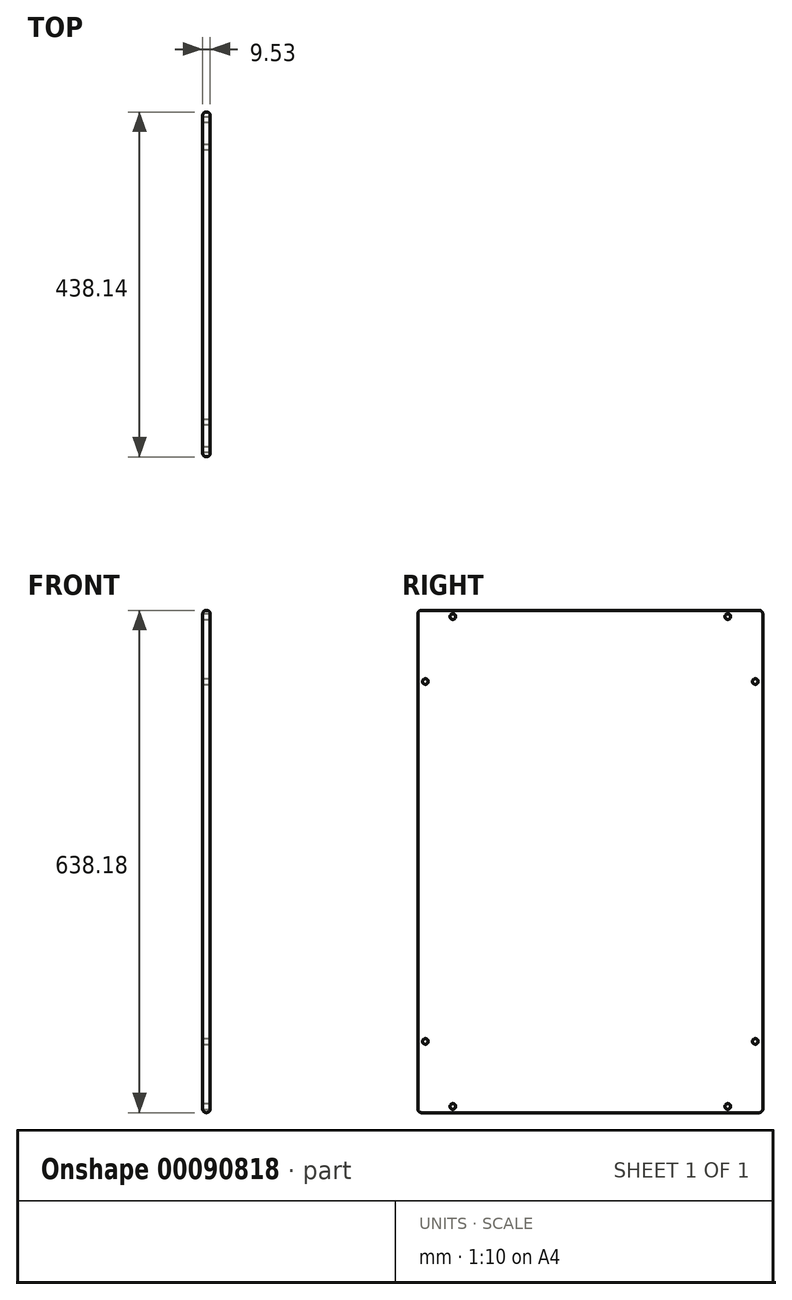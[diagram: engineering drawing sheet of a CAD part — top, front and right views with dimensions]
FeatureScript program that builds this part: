
annotation { "Feature Type Name" : "Feature", "Feature Type Description" : "" }
export const myFeature = defineFeature(function(context is Context, id is Id, definition is map)
    precondition{}
    {
        {
            var Q0;
            Q0=qCreatedBy(makeId("Right.planeOp"),FACE);
            var sketch = newSketch(context, id + "F0", { "sketchPlane" : qUnion([Q0])});
            skLineSegment(sketch, "E0.bottom", {"start": v(219.08, -319.09) * mm, "end": v(-219.07, -319.09) * mm});
            skLineSegment(sketch, "E0.top", {"start": v(219.07, 319.09) * mm, "end": v(-219.08, 319.09) * mm});
            skLineSegment(sketch, "E0.left", {"start": v(219.08, -319.09) * mm, "end": v(219.07, 319.09) * mm});
            skLineSegment(sketch, "E0.right", {"start": v(-219.07, -319.09) * mm, "end": v(-219.08, 319.09) * mm});
            skPoint(sketch, "E0.middle", {"position": v(0, 0) * mm});
            skSolve(sketch);
        }
        {
            var Q0;
            Q0=makeQuery(id+"F0.imprint","IMPRINT",FACE,{"disambiguationData":[TD([[makeQuery(id+"F0.imprint","IMPRINT",EDGE,{"derivedFrom":sQuery(id+"F0.wireOp",EDGE,"E0.bottom")}),-1.0]])]});
            extrude(context, id + "F1", {"entities" : qUnion([Q0]), "depth" : 9.52 * mm});
        }
        {
            var Q0;
            Q0=makeQuery(id+"F1.opExtrude","CAP_FACE",FACE,{"disambiguationData":[OSD([sQuery(id+"F0.wireOp",EDGE,"E0.bottom"),sQuery(id+"F0.wireOp",EDGE,"E0.top"),sQuery(id+"F0.wireOp",EDGE,"E0.left"),sQuery(id+"F0.wireOp",EDGE,"E0.right")])],"isStart":false});
            var sketch = newSketch(context, id + "F2", { "sketchPlane" : qUnion([Q0])});
            skLineSegment(sketch, "E1", {"start": v(0, 319.09) * mm, "end": v(0, -319.09) * mm, "construction": true});
            skPoint(sketch, "E2", {"position": v(-174.63, 311.15) * mm});
            skPoint(sketch, "E3", {"position": v(-209.55, 228.6) * mm});
            skLineSegment(sketch, "E4", {"start": v(-219.07, 0) * mm, "end": v(219.08, 0) * mm, "construction": true});
            skPoint(sketch, "E5.MirrorP", {"position": v(-209.55, -228.6) * mm});
            skPoint(sketch, "E6.MirrorP", {"position": v(-174.62, -311.15) * mm});
            skPoint(sketch, "E7.MirrorP", {"position": v(174.63, 311.15) * mm});
            skPoint(sketch, "E8.MirrorP", {"position": v(209.55, 228.6) * mm});
            skPoint(sketch, "E9.MirrorP", {"position": v(209.55, -228.6) * mm});
            skPoint(sketch, "E10.MirrorP", {"position": v(174.63, -311.15) * mm});
            skSolve(sketch);
        }
        {
            var Q0;
            Q0=sQuery(id+"F2.wireOp",VERTEX,"E2");
            var Q1;
            Q1=sQuery(id+"F2.wireOp",VERTEX,"E3");
            var Q2;
            Q2=sQuery(id+"F2.wireOp",VERTEX,"E5.MirrorP");
            var Q3;
            Q3=sQuery(id+"F2.wireOp",VERTEX,"E6.MirrorP");
            var Q4;
            Q4=sQuery(id+"F2.wireOp",VERTEX,"E10.MirrorP");
            var Q5;
            Q5=sQuery(id+"F2.wireOp",VERTEX,"E9.MirrorP");
            var Q6;
            Q6=sQuery(id+"F2.wireOp",VERTEX,"E7.MirrorP");
            var Q7;
            Q7=sQuery(id+"F2.wireOp",VERTEX,"E8.MirrorP");
            var Q8;
            Q8=makeQuery(id+"F1.opExtrude","SWEPT_BODY",BODY,{"disambiguationData":[OSD([sQuery(id+"F0.wireOp",EDGE,"E0.bottom"),sQuery(id+"F0.wireOp",EDGE,"E0.top"),sQuery(id+"F0.wireOp",EDGE,"E0.left"),sQuery(id+"F0.wireOp",EDGE,"E0.right")])]});
            hole(context, id + "F3", {"style" : HoleStyle.SIMPLE, "endStyle" : HoleEndStyle.THROUGH, "holeDiameter" : 7.14 * mm, "startFromSketch" : true, "locations" : qUnion([Q0, Q1, Q2, Q3, Q4, Q5, Q6, Q7]), "scope" : qUnion([Q8]), "isTappedThrough" : true});
        }
        {
            var Q0;
            Q0=makeQuery(id+"F1.opExtrude","CAP_EDGE",EDGE,{"disambiguationData":[OSD([sQuery(id+"F0.wireOp",EDGE,"E0.right")])],"isStart":true});
            var Q1;
            Q1=makeQuery(id+"F1.opExtrude","CAP_EDGE",EDGE,{"disambiguationData":[OSD([sQuery(id+"F0.wireOp",EDGE,"E0.right")])],"isStart":false});
            var Q2;
            Q2=makeQuery(id+"F1.opExtrude","CAP_EDGE",EDGE,{"disambiguationData":[OSD([sQuery(id+"F0.wireOp",EDGE,"E0.top")])],"isStart":false});
            var Q3;
            Q3=makeQuery(id+"F1.opExtrude","CAP_EDGE",EDGE,{"disambiguationData":[OSD([sQuery(id+"F0.wireOp",EDGE,"E0.top")])],"isStart":true});
            var Q4;
            Q4=makeQuery(id+"F1.opExtrude","SWEPT_EDGE",EDGE,{"disambiguationData":[OSD([sQuery(id+"F0.wireOp",EDGE,"E0.top"),sQuery(id+"F0.wireOp",EDGE,"E0.right")])]});
            var Q5;
            Q5=makeQuery(id+"F1.opExtrude","SWEPT_EDGE",EDGE,{"disambiguationData":[OSD([sQuery(id+"F0.wireOp",EDGE,"E0.top"),sQuery(id+"F0.wireOp",EDGE,"E0.left")])]});
            var Q6;
            Q6=makeQuery(id+"F1.opExtrude","CAP_EDGE",EDGE,{"disambiguationData":[OSD([sQuery(id+"F0.wireOp",EDGE,"E0.left")])],"isStart":true});
            var Q7;
            Q7=makeQuery(id+"F1.opExtrude","CAP_EDGE",EDGE,{"disambiguationData":[OSD([sQuery(id+"F0.wireOp",EDGE,"E0.left")])],"isStart":false});
            var Q8;
            Q8=makeQuery(id+"F1.opExtrude","CAP_EDGE",EDGE,{"disambiguationData":[OSD([sQuery(id+"F0.wireOp",EDGE,"E0.bottom")])],"isStart":true});
            var Q9;
            Q9=makeQuery(id+"F1.opExtrude","CAP_EDGE",EDGE,{"disambiguationData":[OSD([sQuery(id+"F0.wireOp",EDGE,"E0.bottom")])],"isStart":false});
            var Q10;
            Q10=makeQuery(id+"F1.opExtrude","SWEPT_EDGE",EDGE,{"disambiguationData":[OSD([sQuery(id+"F0.wireOp",EDGE,"E0.bottom"),sQuery(id+"F0.wireOp",EDGE,"E0.right")])]});
            var Q11;
            Q11=makeQuery(id+"F1.opExtrude","SWEPT_EDGE",EDGE,{"disambiguationData":[OSD([sQuery(id+"F0.wireOp",EDGE,"E0.bottom"),sQuery(id+"F0.wireOp",EDGE,"E0.left")])]});
            fillet(context, id + "F4", {"entities" : qUnion([Q0, Q1, Q2, Q3, Q4, Q5, Q6, Q7, Q8, Q9, Q10, Q11]), "radius" : 4.76 * mm, "tangentPropagation" : true, "allowEdgeOverflow" : false});
        }
    });
